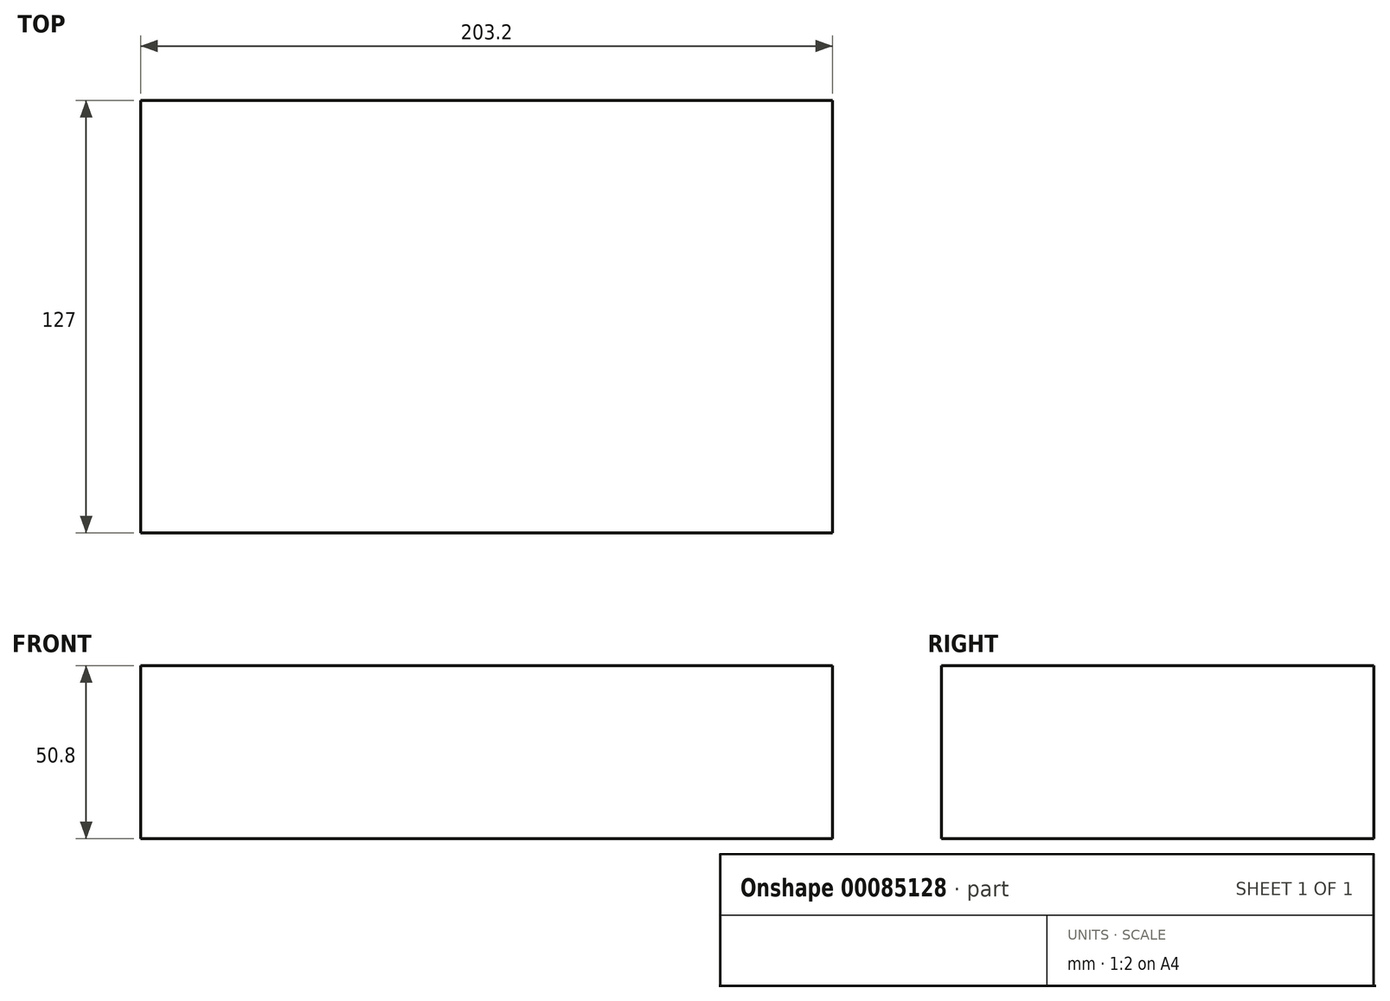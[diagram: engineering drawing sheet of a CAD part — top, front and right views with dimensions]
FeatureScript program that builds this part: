
annotation { "Feature Type Name" : "Feature", "Feature Type Description" : "" }
export const myFeature = defineFeature(function(context is Context, id is Id, definition is map)
    precondition{}
    {
        {
            var Q0;
            Q0=qCreatedBy(makeId("Top.planeOp"),FACE);
            var sketch = newSketch(context, id + "F0", { "sketchPlane" : qUnion([Q0])});
            skLineSegment(sketch, "E0.bottom", {"start": v(0, 0) * mm, "end": v(203.2, 0) * mm});
            skLineSegment(sketch, "E0.top", {"start": v(0, 127) * mm, "end": v(203.2, 127) * mm});
            skLineSegment(sketch, "E0.left", {"start": v(0, 0) * mm, "end": v(0, 127) * mm});
            skLineSegment(sketch, "E0.right", {"start": v(203.2, 0) * mm, "end": v(203.2, 127) * mm});
            skSolve(sketch);
        }
        {
            var Q0;
            Q0 = qSketchRegion(id + "F0", true);
            extrude(context, id + "F1", {"entities" : qUnion([Q0]), "depth" : 50.8 * mm});
        }
    });
